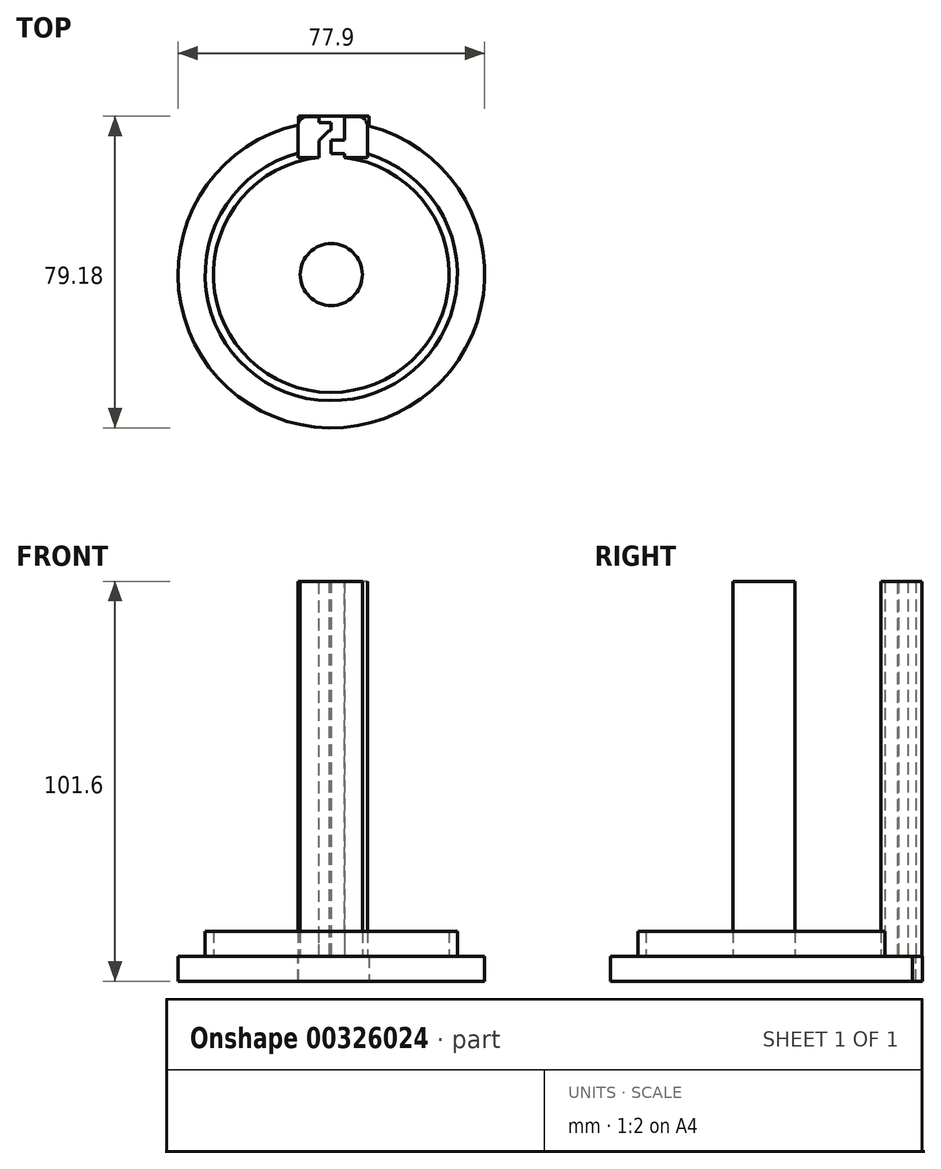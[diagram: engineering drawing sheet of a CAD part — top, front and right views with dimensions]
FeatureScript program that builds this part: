
annotation { "Feature Type Name" : "Feature", "Feature Type Description" : "" }
export const myFeature = defineFeature(function(context is Context, id is Id, definition is map)
    precondition{}
    {
        {
            var Q0;
            Q0=qCreatedBy(makeId("Top.planeOp"),FACE);
            var sketch = newSketch(context, id + "F0", { "sketchPlane" : qUnion([Q0])});
            skCircle(sketch, "E0", {"center": v(0, 0) * mm, "radius": 7.89 * mm});
            skSolve(sketch);
        }
        {
            var Q0;
            Q0=qCreatedBy(makeId("Top.planeOp"),FACE);
            var sketch = newSketch(context, id + "F1", { "sketchPlane" : qUnion([Q0])});
            skCircle(sketch, "E1", {"center": v(0, 0) * mm, "radius": 38.95 * mm});
            skSolve(sketch);
        }
        {
            var Q0;
            Q0 = qSketchRegion(id + "F1", true);
            extrude(context, id + "F2", {"entities" : qUnion([Q0]), "depth" : 6.35 * mm, "offsetDistance" : 25.4 * mm});
        }
        {
            var Q0;
            Q0=makeQuery(id+"F0.imprint","IMPRINT",FACE,{"disambiguationData":[TD([[makeQuery(id+"F0.imprint","IMPRINT",EDGE,{"derivedFrom":sQuery(id+"F0.wireOp",EDGE,"E0")}),1.0]])]});
            extrude(context, id + "F3", {"entities" : qUnion([Q0]), "operationType" : NewBodyOperationType.ADD, "depth" : 101.6 * mm, "offsetDistance" : 25.4 * mm});
        }
        {
            var Q0;
            Q0=qCreatedBy(makeId("Top.planeOp"),FACE);
            var sketch = newSketch(context, id + "F4", { "sketchPlane" : qUnion([Q0])});
            skCircle(sketch, "E2", {"center": v(0, 0) * mm, "radius": 32.04 * mm});
            skCircle(sketch, "E3", {"center": v(0, 0) * mm, "radius": 29.94 * mm});
            skSolve(sketch);
        }
        {
            var Q0;
            Q0=makeQuery(id+"F4.imprint","IMPRINT",FACE,{"disambiguationData":[TD([[makeQuery(id+"F4.imprint","IMPRINT",EDGE,{"derivedFrom":sQuery(id+"F4.wireOp",EDGE,"E2")}),1.0]])]});
            extrude(context, id + "F5", {"entities" : qUnion([Q0]), "operationType" : NewBodyOperationType.ADD, "depth" : 12.7 * mm, "offsetDistance" : 25.4 * mm});
        }
        {
            var Q0;
            Q0=qCreatedBy(makeId("Top.planeOp"),FACE);
            var sketch = newSketch(context, id + "F6", { "sketchPlane" : qUnion([Q0])});
            skLineSegment(sketch, "E4.bottom", {"start": v(-8.47, 40.2) * mm, "end": v(9.2, 40.2) * mm});
            skLineSegment(sketch, "E4.top", {"start": v(-8.47, 29.77) * mm, "end": v(9.2, 29.77) * mm});
            skLineSegment(sketch, "E4.left", {"start": v(-8.47, 40.2) * mm, "end": v(-8.47, 29.77) * mm});
            skLineSegment(sketch, "E4.right", {"start": v(9.2, 40.2) * mm, "end": v(9.2, 29.77) * mm});
            skSolve(sketch);
        }
        {
            var Q0;
            Q0=makeQuery(id+"F6.imprint","IMPRINT",FACE,{"disambiguationData":[TD([[makeQuery(id+"F6.imprint","IMPRINT",EDGE,{"derivedFrom":sQuery(id+"F6.wireOp",EDGE,"E4.bottom")}),-1.0]])]});
            extrude(context, id + "F7", {"entities" : qUnion([Q0]), "operationType" : NewBodyOperationType.ADD, "depth" : 101.6 * mm, "offsetDistance" : 25.4 * mm});
        }
        {
            var Q0;
            Q0=makeQuery(id+"F7.opExtrude","SWEPT_EDGE",EDGE,{"disambiguationData":[OSD([sQuery(id+"F6.wireOp",EDGE,"E4.bottom"),sQuery(id+"F6.wireOp",EDGE,"E4.right")])]});
            fillet(context, id + "F8", {"entities" : qUnion([Q0]), "radius" : 2.54 * mm, "tangentPropagation" : true, "allowEdgeOverflow" : false});
        }
        {
            var Q0;
            Q0=makeQuery(id+"F7.opExtrude","SWEPT_EDGE",EDGE,{"disambiguationData":[OSD([sQuery(id+"F6.wireOp",EDGE,"E4.bottom"),sQuery(id+"F6.wireOp",EDGE,"E4.left")])]});
            fillet(context, id + "F9", {"entities" : qUnion([Q0]), "radius" : 2.54 * mm, "tangentPropagation" : true, "allowEdgeOverflow" : false});
        }
        {
            var Q0;
            Q0=qCreatedBy(makeId("Top.planeOp"),FACE);
            var sketch = newSketch(context, id + "F10", { "sketchPlane" : qUnion([Q0])});
            skLineSegment(sketch, "E5.bottom", {"start": v(3.42, 28.98) * mm, "end": v(-3.16, 28.98) * mm});
            skLineSegment(sketch, "E5.top", {"start": v(3.42, 40.29) * mm, "end": v(-3.16, 40.29) * mm});
            skLineSegment(sketch, "E5.left", {"start": v(3.42, 28.98) * mm, "end": v(3.42, 40.29) * mm});
            skLineSegment(sketch, "E5.right", {"start": v(-3.16, 28.98) * mm, "end": v(-3.16, 40.29) * mm});
            skSolve(sketch);
        }
        {
            var Q0;
            Q0=makeQuery(id+"F10.imprint","IMPRINT",FACE,{"disambiguationData":[TD([[makeQuery(id+"F10.imprint","IMPRINT",EDGE,{"derivedFrom":sQuery(id+"F10.wireOp",EDGE,"E5.bottom")}),-1.0]])]});
            extrude(context, id + "F11", {"entities" : qUnion([Q0]), "operationType" : NewBodyOperationType.REMOVE, "depth" : 101.6 * mm, "offsetDistance" : 25.4 * mm});
        }
        {
            var Q0;
            Q0=qCreatedBy(makeId("Top.planeOp"),FACE);
            var sketch = newSketch(context, id + "F12", { "sketchPlane" : qUnion([Q0])});
            skLineSegment(sketch, "E6.bottom", {"start": v(3.42, 30.76) * mm, "end": v(0, 30.76) * mm});
            skLineSegment(sketch, "E6.top", {"start": v(3.42, 34.18) * mm, "end": v(0, 34.18) * mm});
            skLineSegment(sketch, "E6.left", {"start": v(3.42, 30.76) * mm, "end": v(3.42, 34.18) * mm});
            skLineSegment(sketch, "E6.right", {"start": v(0, 30.76) * mm, "end": v(0, 34.18) * mm});
            skLineSegment(sketch, "E7.bottom", {"start": v(-3.16, 38.65) * mm, "end": v(0, 38.65) * mm});
            skLineSegment(sketch, "E7.top", {"start": v(-3.16, 36.55) * mm, "end": v(0, 36.55) * mm});
            skLineSegment(sketch, "E7.left", {"start": v(-3.16, 38.65) * mm, "end": v(-3.16, 36.55) * mm});
            skLineSegment(sketch, "E7.right", {"start": v(0, 38.65) * mm, "end": v(0, 36.55) * mm});
            skSolve(sketch);
        }
        {
            var Q0;
            Q0=makeQuery(id+"F12.imprint","IMPRINT",FACE,{"disambiguationData":[TD([[makeQuery(id+"F12.imprint","IMPRINT",EDGE,{"derivedFrom":sQuery(id+"F12.wireOp",EDGE,"E6.bottom")}),-1.0]])]});
            var Q1;
            Q1=makeQuery(id+"F12.imprint","IMPRINT",FACE,{"disambiguationData":[TD([[makeQuery(id+"F12.imprint","IMPRINT",EDGE,{"derivedFrom":sQuery(id+"F12.wireOp",EDGE,"E7.bottom")}),-1.0]])]});
            extrude(context, id + "F13", {"entities" : qUnion([Q0, Q1]), "operationType" : NewBodyOperationType.ADD, "depth" : 101.6 * mm});
        }
        {
            var Q0;
            Q0=makeQuery(id+"F13.opExtrude","SWEPT_EDGE",EDGE,{"disambiguationData":[OSD([sQuery(id+"F12.wireOp",EDGE,"E6.top"),sQuery(id+"F12.wireOp",EDGE,"E6.left")])]});
            var Q1;
            Q1=makeQuery(id+"F13.opExtrude","SWEPT_EDGE",EDGE,{"disambiguationData":[OSD([sQuery(id+"F12.wireOp",EDGE,"E7.top"),sQuery(id+"F12.wireOp",EDGE,"E7.left")])]});
            chamfer(context, id + "F14", {"entities" : qUnion([Q0, Q1]), "width" : 2.54 * mm, "tangentPropagation" : true});
        }
        {
            var Q0;
            Q0=qCreatedBy(makeId("Top.planeOp"),FACE);
            var sketch = newSketch(context, id + "F15", { "sketchPlane" : qUnion([Q0])});
            skLineSegment(sketch, "E8.bottom", {"start": v(9.6, 28.66) * mm, "end": v(-8.28, 28.66) * mm});
            skLineSegment(sketch, "E8.top", {"start": v(9.6, 40.23) * mm, "end": v(-8.28, 40.23) * mm});
            skLineSegment(sketch, "E8.left", {"start": v(9.6, 28.66) * mm, "end": v(9.6, 40.23) * mm});
            skLineSegment(sketch, "E8.right", {"start": v(-8.28, 28.66) * mm, "end": v(-8.28, 40.23) * mm});
            skSolve(sketch);
        }
        {
            var Q0;
            Q0 = qSketchRegion(id + "F15", true);
            extrude(context, id + "F16", {"entities" : qUnion([Q0]), "operationType" : NewBodyOperationType.ADD, "depth" : 6.35 * mm});
        }
    });
